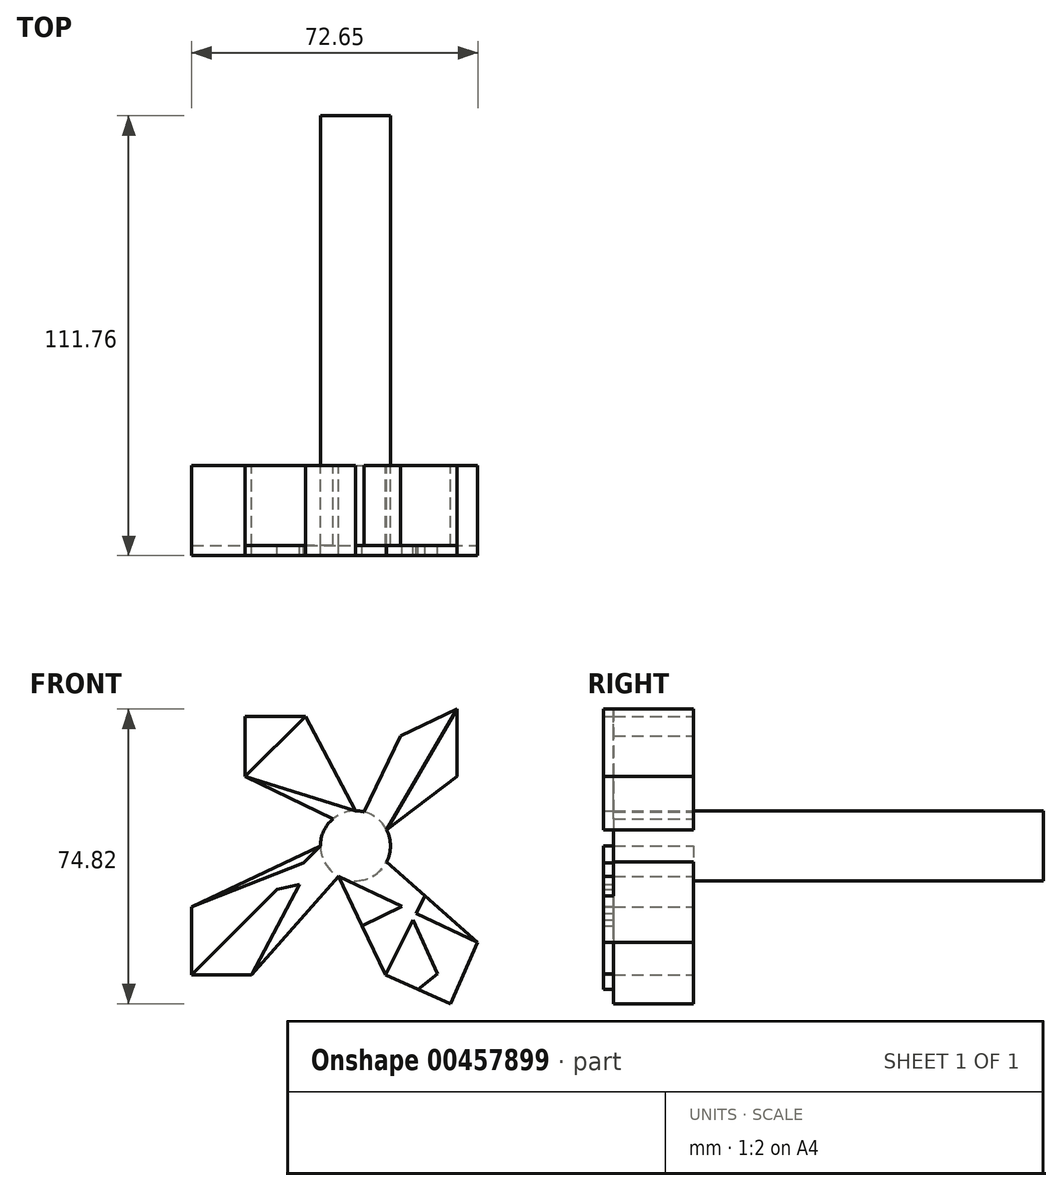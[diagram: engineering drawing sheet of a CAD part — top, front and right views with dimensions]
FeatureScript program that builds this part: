
annotation { "Feature Type Name" : "Feature", "Feature Type Description" : "" }
export const myFeature = defineFeature(function(context is Context, id is Id, definition is map)
    precondition{}
    {
        {
            var Q0;
            Q0=qCreatedBy(makeId("Front.planeOp"),FACE);
            var sketch = newSketch(context, id + "F0", { "sketchPlane" : qUnion([Q0])});
            skCircle(sketch, "E0", {"center": v(0, 0) * mm, "radius": 8.9 * mm});
            skSolve(sketch);
        }
        {
            var Q0;
            Q0 = qSketchRegion(id + "F0", true);
            extrude(context, id + "F1", {"entities" : qUnion([Q0]), "depth" : 88.9 * mm, "offsetDistance" : 25.4 * mm});
        }
        {
            var Q0;
            Q0=makeQuery(id+"F1.opExtrude","CAP_FACE",FACE,{"disambiguationData":[OSD([sQuery(id+"F0.wireOp",EDGE,"E0")])],"isStart":false});
            var sketch = newSketch(context, id + "F2", { "sketchPlane" : qUnion([Q0])});
            skLineSegment(sketch, "E1", {"start": v(-8.89, 0) * mm, "end": v(-41.57, -15.55) * mm});
            skLineSegment(sketch, "E2", {"start": v(-41.57, -15.55) * mm, "end": v(-41.57, -32.8) * mm});
            skLineSegment(sketch, "E3", {"start": v(-41.57, -32.8) * mm, "end": v(-26.42, -32.8) * mm});
            skLineSegment(sketch, "E4", {"start": v(-26.42, -32.8) * mm, "end": v(-4.3, -7.79) * mm});
            skLineSegment(sketch, "E5", {"start": v(-4.3, -7.79) * mm, "end": v(7.6, -32.8) * mm});
            skLineSegment(sketch, "E6", {"start": v(7.6, -32.8) * mm, "end": v(24.2, -40.1) * mm});
            skLineSegment(sketch, "E7", {"start": v(24.2, -40.1) * mm, "end": v(31.08, -24.53) * mm});
            skLineSegment(sketch, "E8", {"start": v(31.08, -24.53) * mm, "end": v(7.92, -4.03) * mm});
            skLineSegment(sketch, "E9", {"start": v(-5.74, 6.79) * mm, "end": v(-28.01, 17.58) * mm});
            skLineSegment(sketch, "E10", {"start": v(-28.01, 17.58) * mm, "end": v(-28.01, 32.9) * mm});
            skLineSegment(sketch, "E11", {"start": v(-28.01, 32.9) * mm, "end": v(-12.72, 32.9) * mm});
            skLineSegment(sketch, "E12", {"start": v(-12.72, 32.9) * mm, "end": v(0, 8.9) * mm});
            skLineSegment(sketch, "E13", {"start": v(2.15, 8.63) * mm, "end": v(11.5, 27.93) * mm});
            skLineSegment(sketch, "E14", {"start": v(11.5, 27.93) * mm, "end": v(25.77, 34.71) * mm});
            skLineSegment(sketch, "E15", {"start": v(25.77, 34.71) * mm, "end": v(25.77, 17.63) * mm});
            skLineSegment(sketch, "E16", {"start": v(25.77, 17.63) * mm, "end": v(7.92, 4.03) * mm});
            skSolve(sketch);
        }
        {
            var Q0;
            {var subQ0=makeQuery(id+"F1.opExtrude","CAP_EDGE",EDGE,{"disambiguationData":[OSD([sQuery(id+"F0.wireOp",EDGE,"E0")])],"isStart":false});var subQ1=makeQuery(id+"F2.imprint","INTERSECT",VERTEX,{"derivedFrom":[subQ0,sQuery(id+"F2.wireOp",EDGE,"E1")]});Q0=makeQuery(id+"F2.imprint","IMPRINT",FACE,{"disambiguationData":[TD([[makeQuery(id+"F2.imprint","IMPRINT",EDGE,{"disambiguationData":[TD([[subQ1,1.0]])],"derivedFrom":subQ0}),1.0]])]});}
            var sketch = newSketch(context, id + "F3", { "sketchPlane" : qUnion([Q0])});
            skSolve(sketch);
        }
        {
            var Q0;
            Q0 = qSketchRegion(id + "F3", true);
            var Q1;
            {var subQ1=sQuery(id+"F2.wireOp",EDGE,"E1");Q1=makeQuery(id+"F2.imprint","IMPRINT",FACE,{"disambiguationData":[TD([[makeQuery(id+"F2.imprint","IMPRINT",EDGE,{"derivedFrom":subQ1}),1.0]])]});}
            var Q2;
            {var subQ1=sQuery(id+"F2.wireOp",EDGE,"E5");Q2=makeQuery(id+"F2.imprint","IMPRINT",FACE,{"disambiguationData":[TD([[makeQuery(id+"F2.imprint","IMPRINT",EDGE,{"derivedFrom":subQ1}),1.0]])]});}
            var Q3;
            {var subQ1=sQuery(id+"F2.wireOp",EDGE,"E13");Q3=makeQuery(id+"F2.imprint","IMPRINT",FACE,{"disambiguationData":[TD([[makeQuery(id+"F2.imprint","IMPRINT",EDGE,{"derivedFrom":subQ1}),-1.0]])]});}
            var Q4;
            {var subQ1=sQuery(id+"F2.wireOp",EDGE,"E9");Q4=makeQuery(id+"F2.imprint","IMPRINT",FACE,{"disambiguationData":[TD([[makeQuery(id+"F2.imprint","IMPRINT",EDGE,{"derivedFrom":subQ1}),-1.0]])]});}
            var Q5;
            {var subQ0=makeQuery(id+"F1.opExtrude","CAP_EDGE",EDGE,{"disambiguationData":[OSD([sQuery(id+"F0.wireOp",EDGE,"E0")])],"isStart":false});var subQ1=makeQuery(id+"F2.imprint","INTERSECT",VERTEX,{"derivedFrom":[subQ0,sQuery(id+"F2.wireOp",EDGE,"E1")]});Q5=makeQuery(id+"F2.imprint","IMPRINT",FACE,{"disambiguationData":[TD([[makeQuery(id+"F2.imprint","IMPRINT",EDGE,{"disambiguationData":[TD([[subQ1,1.0]])],"derivedFrom":subQ0}),1.0]])]});}
            extrude(context, id + "F4", {"entities" : qUnion([Q0, Q1, Q2, Q3, Q4, Q5]), "operationType" : NewBodyOperationType.ADD, "depth" : 20.32 * mm, "offsetDistance" : 25.4 * mm});
        }
        {
            var Q0;
            Q0=makeQuery(id+"F4.opExtrude","CAP_FACE",FACE,{"disambiguationData":[OSD([sQuery(id+"F0.wireOp",EDGE,"E0"),sQuery(id+"F2.wireOp",EDGE,"E1"),sQuery(id+"F2.wireOp",EDGE,"E2"),sQuery(id+"F2.wireOp",EDGE,"E3"),sQuery(id+"F2.wireOp",EDGE,"E4"),sQuery(id+"F2.wireOp",EDGE,"E5"),sQuery(id+"F2.wireOp",EDGE,"E6"),sQuery(id+"F2.wireOp",EDGE,"E7"),sQuery(id+"F2.wireOp",EDGE,"E8"),sQuery(id+"F2.wireOp",EDGE,"E9"),sQuery(id+"F2.wireOp",EDGE,"E10"),sQuery(id+"F2.wireOp",EDGE,"E11"),sQuery(id+"F2.wireOp",EDGE,"E12"),sQuery(id+"F2.wireOp",EDGE,"E13"),sQuery(id+"F2.wireOp",EDGE,"E14"),sQuery(id+"F2.wireOp",EDGE,"E15"),sQuery(id+"F2.wireOp",EDGE,"E16")])],"isStart":false});
            var sketch = newSketch(context, id + "F5", { "sketchPlane" : qUnion([Q0])});
            skLineSegment(sketch, "E17", {"start": v(15.9, -36.45) * mm, "end": v(31.08, -24.53) * mm});
            skLineSegment(sketch, "E18", {"start": v(1.66, -20.29) * mm, "end": v(17.68, -12.67) * mm});
            skPoint(sketch, "E19.startSnap0", {"position": v(-6.36, 20.9) * mm});
            skPoint(sketch, "E19.startSnap1", {"position": v(6.83, 18.28) * mm});
            skLineSegment(sketch, "E20", {"start": v(7.6, -32.8) * mm, "end": v(17.68, -12.67) * mm});
            skLineSegment(sketch, "E21", {"start": v(-4.3, -7.79) * mm, "end": v(7.92, -4.03) * mm});
            skLineSegment(sketch, "E22", {"start": v(7.92, -4.03) * mm, "end": v(24.2, -40.1) * mm});
            skLineSegment(sketch, "E23", {"start": v(24.2, -40.1) * mm, "end": v(7.92, -4.03) * mm});
            skLineSegment(sketch, "E24", {"start": v(7.6, -32.8) * mm, "end": v(-4.3, -7.79) * mm});
            skLineSegment(sketch, "E25", {"start": v(-4.3, -7.79) * mm, "end": v(31.08, -24.53) * mm});
            skLineSegment(sketch, "E26", {"start": v(-41.57, -32.8) * mm, "end": v(25.77, 34.71) * mm});
            skLineSegment(sketch, "E27", {"start": v(25.77, 34.71) * mm, "end": v(7.92, 4.03) * mm});
            skLineSegment(sketch, "E28", {"start": v(7.92, 4.03) * mm, "end": v(-41.57, -15.55) * mm});
            skLineSegment(sketch, "E29", {"start": v(-41.57, -15.55) * mm, "end": v(-26.42, -32.8) * mm});
            skLineSegment(sketch, "E30", {"start": v(-26.42, -32.8) * mm, "end": v(-8.9, 0) * mm});
            skLineSegment(sketch, "E31", {"start": v(-8.9, 0) * mm, "end": v(7.92, -4.03) * mm});
            skLineSegment(sketch, "E32", {"start": v(-28.01, 17.58) * mm, "end": v(-12.72, 32.9) * mm});
            skLineSegment(sketch, "E33", {"start": v(-12.72, 32.9) * mm, "end": v(0, 8.89) * mm});
            skLineSegment(sketch, "E34", {"start": v(0, 8.9) * mm, "end": v(-28.01, 17.58) * mm});
            skLineSegment(sketch, "E35", {"start": v(-28.01, 32.9) * mm, "end": v(0, 8.9) * mm});
            skLineSegment(sketch, "E36", {"start": v(-4.3, -7.79) * mm, "end": v(-41.57, -15.55) * mm});
            skSolve(sketch);
        }
        {
            var Q0;
            {var subQ0=sQuery(id+"F5.wireOp",EDGE,"E17");var subQ1=makeQuery(id+"F4.opExtrude","CAP_EDGE",EDGE,{"disambiguationData":[OSD([sQuery(id+"F2.wireOp",EDGE,"E6")])],"isStart":false});var subQ2=makeQuery(id+"F5.imprint","INTERSECT",VERTEX,{"derivedFrom":[subQ1,subQ0]});Q0=makeQuery(id+"F5.imprint","IMPRINT",FACE,{"disambiguationData":[TD([[makeQuery(id+"F5.imprint","IMPRINT",EDGE,{"disambiguationData":[TD([[subQ2,-1.0]])],"derivedFrom":subQ0}),1.0]])]});}
            var Q1;
            {var subQ0=sQuery(id+"F5.wireOp",EDGE,"E24");var subQ1=sQuery(id+"F5.wireOp",EDGE,"E18");var subQ2=makeQuery(id+"F5.imprint","INTERSECT",VERTEX,{"derivedFrom":[subQ1,subQ0]});Q1=makeQuery(id+"F5.imprint","IMPRINT",FACE,{"disambiguationData":[TD([[makeQuery(id+"F5.imprint","IMPRINT",EDGE,{"disambiguationData":[TD([[subQ2,-1.0]])],"derivedFrom":subQ1}),1.0]])]});}
            var Q2;
            {var subQ0=sQuery(id+"F5.wireOp",EDGE,"E20");var subQ3=sQuery(id+"F5.wireOp",EDGE,"E25");var subQ4=makeQuery(id+"F5.imprint","INTERSECT",VERTEX,{"derivedFrom":[subQ0,subQ3]});Q2=makeQuery(id+"F5.imprint","IMPRINT",FACE,{"disambiguationData":[TD([[makeQuery(id+"F5.imprint","IMPRINT",EDGE,{"disambiguationData":[TD([[subQ4,-1.0]])],"derivedFrom":subQ0}),-1.0]])]});}
            var Q3;
            {var subQ0=sQuery(id+"F5.wireOp",EDGE,"E29");var subQ1=sQuery(id+"F5.wireOp",EDGE,"E26");var subQ2=makeQuery(id+"F5.imprint","INTERSECT",VERTEX,{"derivedFrom":[subQ1,subQ0]});Q3=makeQuery(id+"F5.imprint","IMPRINT",FACE,{"disambiguationData":[TD([[makeQuery(id+"F5.imprint","IMPRINT",EDGE,{"disambiguationData":[TD([[subQ2,-1.0]])],"derivedFrom":subQ1}),-1.0]])]});}
            var Q4;
            {var subQ0=sQuery(id+"F5.wireOp",EDGE,"E33");Q4=makeQuery(id+"F5.imprint","IMPRINT",FACE,{"disambiguationData":[TD([[makeQuery(id+"F5.imprint","IMPRINT",EDGE,{"derivedFrom":subQ0}),-1.0]])]});}
            var Q5;
            Q5=makeQuery(id+"F5.imprint","IMPRINT",FACE,{"disambiguationData":[TD([[makeQuery(id+"F5.imprint","IMPRINT",EDGE,{"derivedFrom":sQuery(id+"F5.wireOp",EDGE,"E27")}),1.0]])]});
            var Q6;
            {var subQ1=makeQuery(id+"F4.opExtrude","CAP_EDGE",EDGE,{"disambiguationData":[OSD([sQuery(id+"F2.wireOp",EDGE,"E3")])],"isStart":false});Q6=makeQuery(id+"F5.imprint","IMPRINT",FACE,{"disambiguationData":[TD([[makeQuery(id+"F5.imprint","IMPRINT",EDGE,{"derivedFrom":subQ1}),1.0]])]});}
            var Q7;
            {var subQ0=sQuery(id+"F5.wireOp",EDGE,"E34");Q7=makeQuery(id+"F5.imprint","IMPRINT",FACE,{"disambiguationData":[TD([[makeQuery(id+"F5.imprint","IMPRINT",EDGE,{"derivedFrom":subQ0}),-1.0]])]});}
            var Q8;
            {var subQ5=sQuery(id+"F2.wireOp",EDGE,"E1");var subQ8=makeQuery(id+"F4.opExtrude","CAP_EDGE",EDGE,{"disambiguationData":[OSD([subQ5])],"isStart":false});Q8=makeQuery(id+"F5.imprint","IMPRINT",FACE,{"disambiguationData":[TD([[makeQuery(id+"F5.imprint","IMPRINT",EDGE,{"derivedFrom":subQ8}),1.0]])]});}
            extrude(context, id + "F6", {"entities" : qUnion([Q0, Q1, Q2, Q3, Q4, Q5, Q6, Q7, Q8]), "operationType" : NewBodyOperationType.ADD, "depth" : 2.54 * mm, "offsetDistance" : 25.4 * mm});
        }
    });
